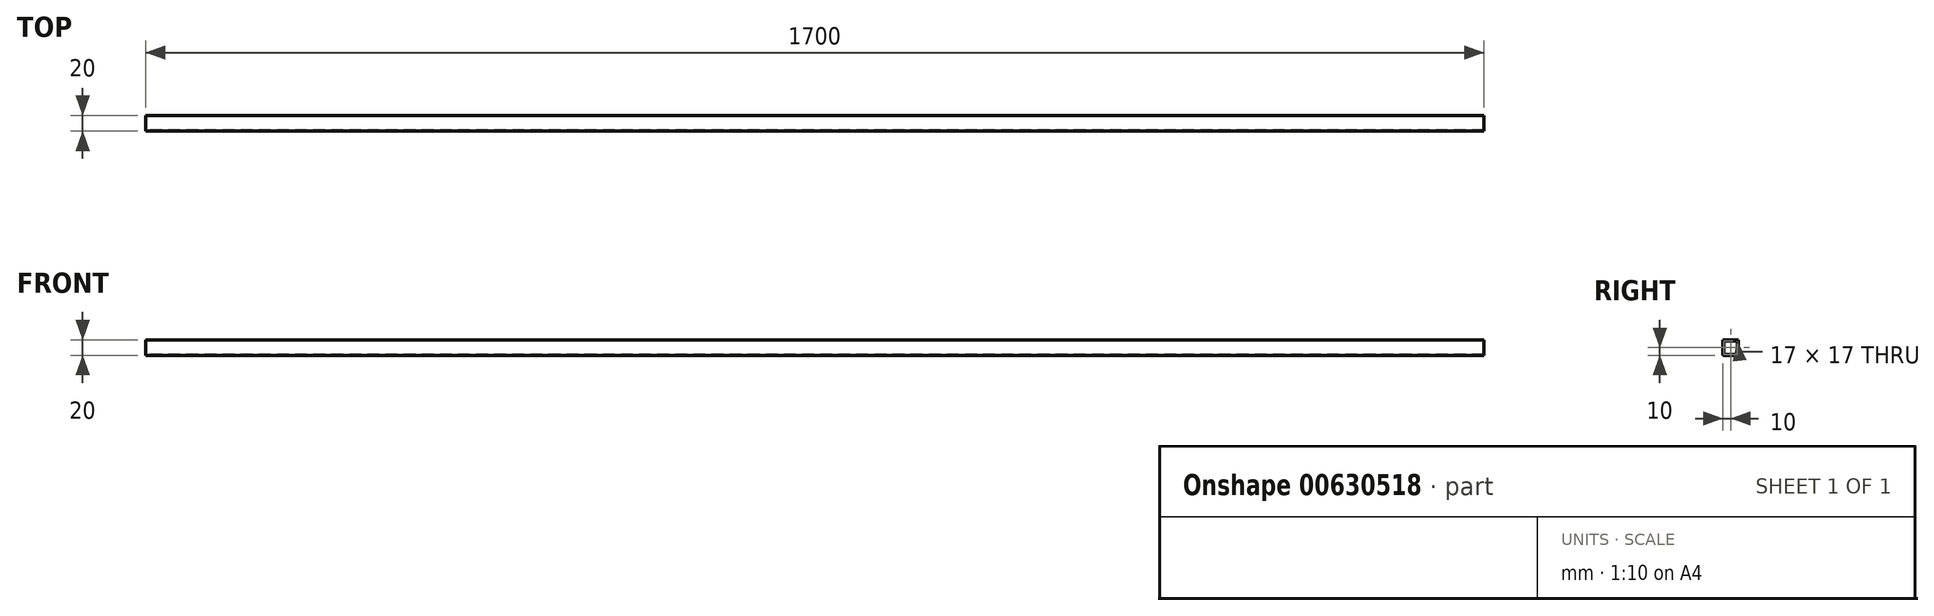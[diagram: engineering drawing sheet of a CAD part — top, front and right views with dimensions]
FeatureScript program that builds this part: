
annotation { "Feature Type Name" : "Feature", "Feature Type Description" : "" }
export const myFeature = defineFeature(function(context is Context, id is Id, definition is map)
    precondition{}
    {
        {
            var Q0;
            Q0=qCreatedBy(makeId("Right.planeOp"),FACE);
            var sketch = newSketch(context, id + "F0", { "sketchPlane" : qUnion([Q0])});
            skLineSegment(sketch, "E0.bottom", {"start": v(-10, 0) * mm, "end": v(10, 0) * mm});
            skLineSegment(sketch, "E0.top", {"start": v(-10, -20) * mm, "end": v(10, -20) * mm});
            skLineSegment(sketch, "E0.left", {"start": v(-10, 0) * mm, "end": v(-10, -20) * mm});
            skLineSegment(sketch, "E0.right", {"start": v(10, 0) * mm, "end": v(10, -20) * mm});
            skLineSegment(sketch, "E1.bottom", {"start": v(-8.5, -1.5) * mm, "end": v(8.5, -1.5) * mm});
            skLineSegment(sketch, "E1.top", {"start": v(-8.5, -18.5) * mm, "end": v(8.5, -18.5) * mm});
            skLineSegment(sketch, "E1.left", {"start": v(-8.5, -1.5) * mm, "end": v(-8.5, -18.5) * mm});
            skLineSegment(sketch, "E1.right", {"start": v(8.5, -1.5) * mm, "end": v(8.5, -18.5) * mm});
            skSolve(sketch);
        }
        {
            var Q0;
            Q0=makeQuery(id+"F0.imprint","IMPRINT",FACE,{"disambiguationData":[TD([[makeQuery(id+"F0.imprint","IMPRINT",EDGE,{"derivedFrom":sQuery(id+"F0.wireOp",EDGE,"E0.bottom")}),-1.0]])]});
            extrude(context, id + "F1", {"entities" : qUnion([Q0]), "depth" : 1700 * mm, "offsetDistance" : 25 * mm});
        }
    });
